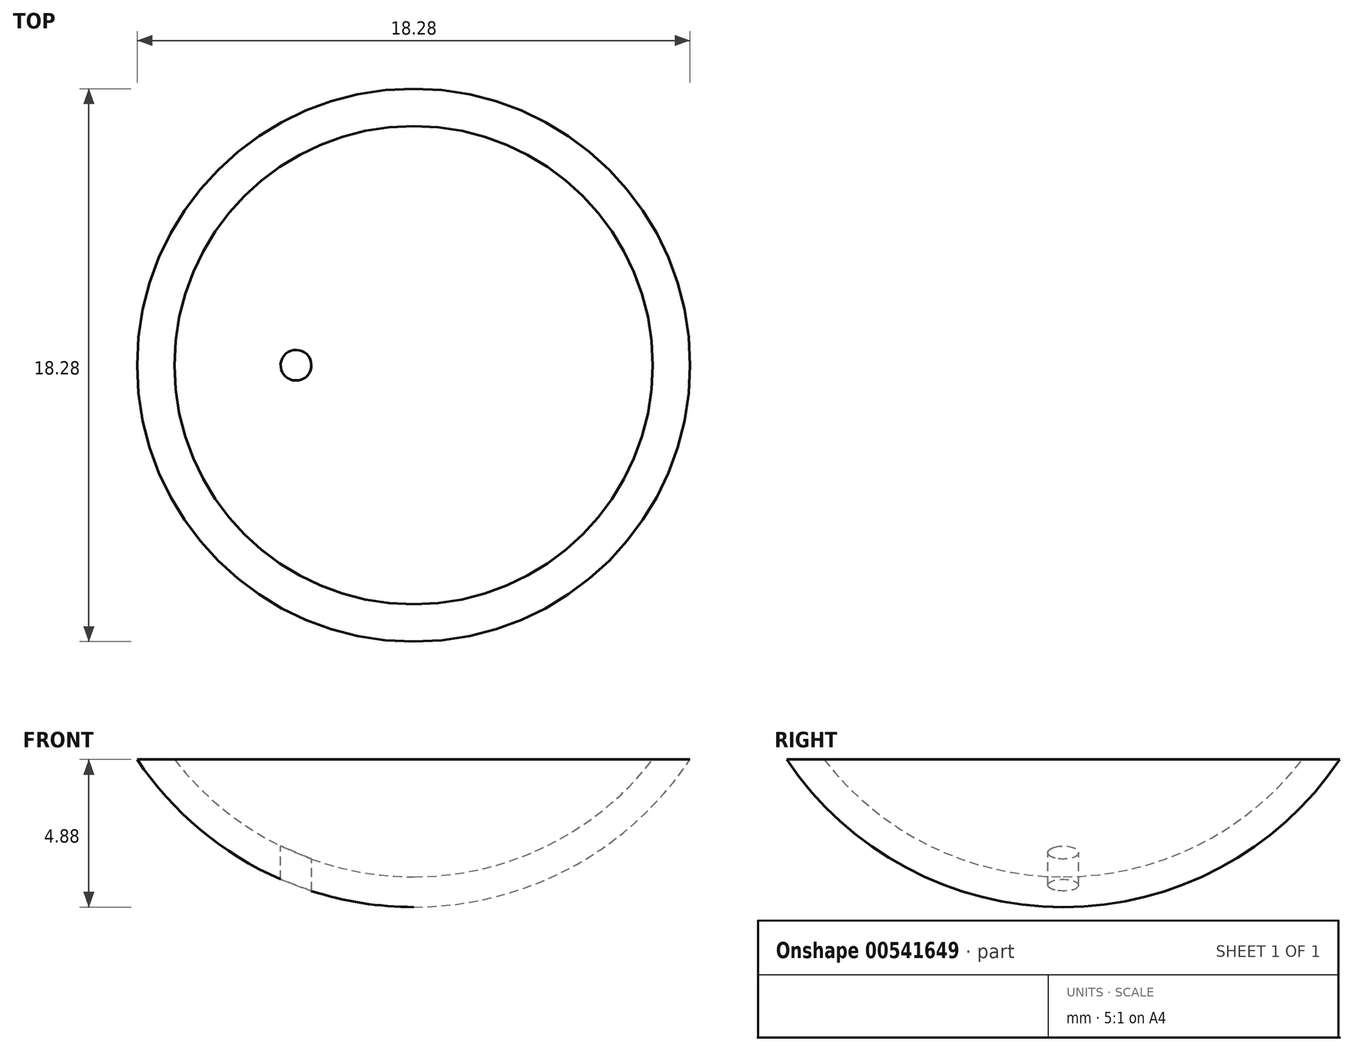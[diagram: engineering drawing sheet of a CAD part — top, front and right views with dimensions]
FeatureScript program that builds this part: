
annotation { "Feature Type Name" : "Feature", "Feature Type Description" : "" }
export const myFeature = defineFeature(function(context is Context, id is Id, definition is map)
    precondition{}
    {
        {
            var Q0;
            Q0=qCreatedBy(makeId("Front.planeOp"),FACE);
            var sketch = newSketch(context, id + "F0", { "sketchPlane" : qUnion([Q0])});
            skCircle(sketch, "E0", {"center": v(0, 0) * mm, "radius": 11 * mm});
            skLineSegment(sketch, "E1", {"start": v(0, 11) * mm, "end": v(0, -11) * mm});
            skLineSegment(sketch, "E2", {"start": v(0, 0) * mm, "end": v(4.89, 0) * mm});
            skSolve(sketch);
        }
        {
            var Q0;
            {var subQ0=sQuery(id+"F0.wireOp",EDGE,"E1");Q0=makeQuery(id+"F0.imprint","IMPRINT",FACE,{"disambiguationData":[TD([[makeQuery(id+"F0.imprint","IMPRINT",EDGE,{"derivedFrom":subQ0}),-1.0]])]});}
            var Q1;
            Q1=sQuery(id+"F0.wireOp",EDGE,"E1");
            revolve(context, id + "F1", {"entities" : qUnion([Q0]), "axis" : qUnion([Q1]), "revolveType" : RevolveType.FULL});
        }
        {
            var Q0;
            Q0=qCreatedBy(makeId("Front.planeOp"),FACE);
            var sketch = newSketch(context, id + "F2", { "sketchPlane" : qUnion([Q0])});
            skLineSegment(sketch, "E3.bottom", {"start": v(-15.41, 16.37) * mm, "end": v(13.36, 16.37) * mm});
            skLineSegment(sketch, "E3.top", {"start": v(-15.41, -15.07) * mm, "end": v(13.36, -15.07) * mm});
            skLineSegment(sketch, "E3.left", {"start": v(-15.41, 16.37) * mm, "end": v(-15.41, -15.07) * mm});
            skLineSegment(sketch, "E3.right", {"start": v(13.36, 16.37) * mm, "end": v(13.36, -15.07) * mm});
            skLineSegment(sketch, "E4", {"start": v(-15.41, -6.12) * mm, "end": v(13.36, -6.12) * mm});
            skSolve(sketch);
        }
        {
            var Q0;
            {var subQ0=sQuery(id+"F2.wireOp",EDGE,"E3.bottom");Q0=makeQuery(id+"F2.imprint","IMPRINT",FACE,{"disambiguationData":[TD([[makeQuery(id+"F2.imprint","IMPRINT",EDGE,{"derivedFrom":subQ0}),-1.0]])]});}
            extrude(context, id + "F3", {"entities" : qUnion([Q0]), "operationType" : NewBodyOperationType.REMOVE, "endBound" : BoundingType.SYMMETRIC, "oppositeDirection" : true, "depth" : 25.4 * mm, "offsetDistance" : 25.4 * mm});
        }
        {
            var Q0;
            Q0=makeQuery(id+"F3.boolean.opBoolean","COPY",FACE,{"derivedFrom":makeQuery(id+"F3.opExtrude","SWEPT_FACE",FACE,{"disambiguationData":[OSD([sQuery(id+"F2.wireOp",EDGE,"E4")])]})});
            shell(context, id + "F4", {"entities" : qUnion([Q0]), "thickness" : 1 * mm});
        }
        {
            var Q0;
            Q0=qCreatedBy(makeId("Top.planeOp"),FACE);
            var sketch = newSketch(context, id + "F5", { "sketchPlane" : qUnion([Q0])});
            skCircle(sketch, "E5", {"center": v(-3.89, 0) * mm, "radius": 0.51 * mm});
            skSolve(sketch);
        }
        {
            var Q0;
            Q0=makeQuery(id+"F5.imprint","IMPRINT",FACE,{"disambiguationData":[TD([[makeQuery(id+"F5.imprint","IMPRINT",EDGE,{"derivedFrom":sQuery(id+"F5.wireOp",EDGE,"E5")}),1.0]])]});
            extrude(context, id + "F6", {"entities" : qUnion([Q0]), "operationType" : NewBodyOperationType.REMOVE, "oppositeDirection" : true, "depth" : 25.4 * mm, "offsetDistance" : 25.4 * mm});
        }
    });
